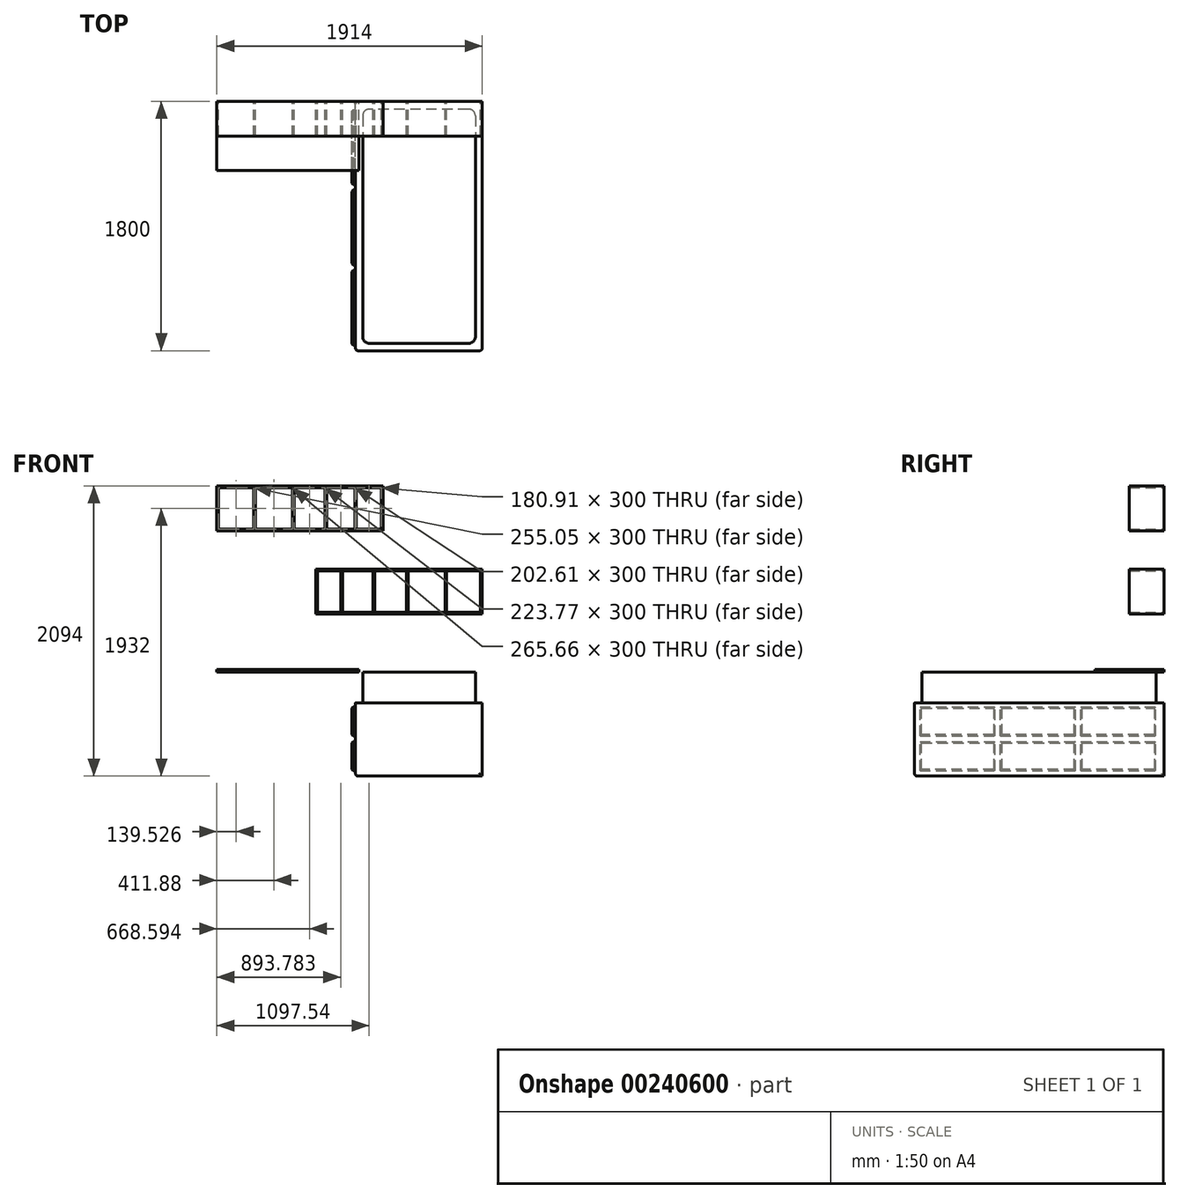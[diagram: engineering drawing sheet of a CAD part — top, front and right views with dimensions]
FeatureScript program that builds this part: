
annotation { "Feature Type Name" : "Feature", "Feature Type Description" : "" }
export const myFeature = defineFeature(function(context is Context, id is Id, definition is map)
    precondition{}
    {
        {
            var Q0;
            Q0=qCreatedBy(makeId("Front.planeOp"),FACE);
            var sketch = newSketch(context, id + "F0", { "sketchPlane" : qUnion([Q0])});
            skLineSegment(sketch, "E0.right", {"start": v(2099, 770) * mm, "end": v(2099, 750) * mm});
            skLineSegment(sketch, "E1.top", {"start": v(2135, 620) * mm, "end": v(2115, 620) * mm});
            skLineSegment(sketch, "E2.bottom", {"start": v(2099, 750) * mm, "end": v(1185, 750) * mm});
            skLineSegment(sketch, "E2.top", {"start": v(2099, 0) * mm, "end": v(1185, 0) * mm});
            skLineSegment(sketch, "E2.left", {"start": v(2099, 750) * mm, "end": v(2099, 0) * mm});
            skLineSegment(sketch, "E2.right", {"start": v(1185, 750) * mm, "end": v(1185, 0) * mm});
            skLineSegment(sketch, "E3.top", {"start": v(2079, 770) * mm, "end": v(2099, 770) * mm});
            skSolve(sketch);
        }
        {
            var Q0;
            {var subQ5=sQuery(id+"F0.wireOp",EDGE,"mjQCl8UT-21zD-DJ05-m4hR-eCqY9wOHKZ8C.bottom");Q0=makeQuery(id+"F0.imprint","IMPRINT",FACE,{"disambiguationData":[TD([[makeQuery(id+"F0.imprint","IMPRINT",EDGE,{"derivedFrom":subQ5}),-1.0]])]});}
            var Q1;
            Q1=makeQuery(id+"F0.imprint","IMPRINT",FACE,{"disambiguationData":[TD([[makeQuery(id+"F0.imprint","IMPRINT",EDGE,{"derivedFrom":sQuery(id+"F0.wireOp",EDGE,"fViOHY5F-jbjT-sDrG-rFHW-0nsrj5jH0THn.bottom")}),1.0]])]});
            var Q2;
            Q2=makeQuery(id+"F0.imprint","IMPRINT",FACE,{"disambiguationData":[TD([[makeQuery(id+"F0.imprint","IMPRINT",EDGE,{"derivedFrom":sQuery(id+"F0.wireOp",EDGE,"CURJZSOY-zp0L-gG35-HGPp-CF3T4XPkt2g1.bottom")}),1.0]])]});
            var Q3;
            Q3=makeQuery(id+"F0.imprint","IMPRINT",FACE,{"disambiguationData":[TD([[makeQuery(id+"F0.imprint","IMPRINT",EDGE,{"derivedFrom":sQuery(id+"F0.wireOp",EDGE,"rYcHEG5W-3RAi-ODDc-aat0-Rc7xTILlibCM.bottom")}),-1.0]])]});
            var Q4;
            {var subQ0=sQuery(id+"F0.wireOp",EDGE,"Hld5sJT8-8Eor-Fkzm-HqOC-IpYSd5zHQiRJ.left");Q4=makeQuery(id+"F0.imprint","IMPRINT",FACE,{"disambiguationData":[TD([[makeQuery(id+"F0.imprint","IMPRINT",EDGE,{"derivedFrom":subQ0}),-1.0]])]});}
            var Q5;
            {var subQ3=sQuery(id+"F0.wireOp",EDGE,"Ef43F33Y-ZOyo-R4mQ-mZii-0W5uo4y5c10D.bottom");Q5=makeQuery(id+"F0.imprint","IMPRINT",FACE,{"disambiguationData":[TD([[makeQuery(id+"F0.imprint","IMPRINT",EDGE,{"derivedFrom":subQ3}),-1.0]])]});}
            var Q6;
            Q6=makeQuery(id+"F0.imprint","IMPRINT",FACE,{"disambiguationData":[TD([[makeQuery(id+"F0.imprint","IMPRINT",EDGE,{"derivedFrom":sQuery(id+"F0.wireOp",EDGE,"NrUvMHko-TrKp-QnW1-jtb7-1sPzA3xdgOMU.bottom")}),-1.0]])]});
            var Q7;
            Q7=makeQuery(id+"F0.imprint","IMPRINT",FACE,{"disambiguationData":[TD([[makeQuery(id+"F0.imprint","IMPRINT",EDGE,{"derivedFrom":sQuery(id+"F0.wireOp",EDGE,"5VmnRn0p-VOUw-hyS7-2uir-4T0axD03U4wE.bottom")}),1.0]])]});
            var Q8;
            {var subQ0=sQuery(id+"F0.wireOp",EDGE,"xXXFPRuC-vsK8-C333-ZqZV-EY1DFygu61gq.bottom");Q8=makeQuery(id+"F0.imprint","IMPRINT",FACE,{"disambiguationData":[TD([[makeQuery(id+"F0.imprint","IMPRINT",EDGE,{"derivedFrom":subQ0}),-1.0]])]});}
            var Q9;
            {var subQ0=sQuery(id+"F0.wireOp",EDGE,"SrouK1QG-l51e-v0bo-YR4G-QEAQBbo4jVZ9.left");Q9=makeQuery(id+"F0.imprint","IMPRINT",FACE,{"disambiguationData":[TD([[makeQuery(id+"F0.imprint","IMPRINT",EDGE,{"derivedFrom":subQ0}),1.0]])]});}
            var Q10;
            {var subQ4=sQuery(id+"F0.wireOp",EDGE,"E3.bottom");Q10=makeQuery(id+"F0.imprint","IMPRINT",FACE,{"disambiguationData":[TD([[makeQuery(id+"F0.imprint","IMPRINT",EDGE,{"derivedFrom":subQ4}),-1.0]])]});}
            var Q11;
            {var subQ5=sQuery(id+"F0.wireOp",EDGE,"E3.top");Q11=makeQuery(id+"F0.imprint","IMPRINT",FACE,{"disambiguationData":[TD([[makeQuery(id+"F0.imprint","IMPRINT",EDGE,{"derivedFrom":subQ5}),1.0]])]});}
            var Q12;
            {var subQ0=sQuery(id+"F0.wireOp",EDGE,"E3.right");var subQ1=sQuery(id+"F0.wireOp",EDGE,"SrouK1QG-l51e-v0bo-YR4G-QEAQBbo4jVZ9.bottom");var subQ2=makeQuery(id+"F0.imprint","INTERSECT",VERTEX,{"derivedFrom":[subQ1,subQ0]});Q12=makeQuery(id+"F0.imprint","IMPRINT",FACE,{"disambiguationData":[TD([[makeQuery(id+"F0.imprint","IMPRINT",EDGE,{"disambiguationData":[TD([[subQ2,1.0]])],"derivedFrom":subQ1}),-1.0]])]});}
            var Q13;
            Q13=makeQuery(id+"F0.imprint","IMPRINT",FACE,{"disambiguationData":[TD([[makeQuery(id+"F0.imprint","IMPRINT",EDGE,{"derivedFrom":sQuery(id+"F0.wireOp",EDGE,"E0.bottom")}),-1.0]])]});
            var Q14;
            Q14=makeQuery(id+"F0.imprint","IMPRINT",FACE,{"disambiguationData":[TD([[makeQuery(id+"F0.imprint","IMPRINT",EDGE,{"derivedFrom":sQuery(id+"F0.wireOp",EDGE,"E2.bottom")}),1.0]])]});
            extrude(context, id + "F1", {"entities" : qUnion([Q0, Q1, Q2, Q3, Q4, Q5, Q6, Q7, Q8, Q9, Q10, Q11, Q12, Q13, Q14]), "depth" : 1800 * mm});
        }
        {
            var Q0;
            Q0=makeQuery(id+"F1.opExtrude","CAP_FACE",FACE,{"disambiguationData":[OSD([sQuery(id+"F0.wireOp",EDGE,"E2.bottom"),sQuery(id+"F0.wireOp",EDGE,"E2.top"),sQuery(id+"F0.wireOp",EDGE,"E2.left"),sQuery(id+"F0.wireOp",EDGE,"E2.right")])],"isStart":true});
            var sketch = newSketch(context, id + "F2", { "sketchPlane" : qUnion([Q0])});
            skLineSegment(sketch, "E4.bottom", {"start": v(-1185, 750) * mm, "end": v(-185, 750) * mm});
            skLineSegment(sketch, "E4.top", {"start": v(-1185, 770) * mm, "end": v(-185, 770) * mm});
            skLineSegment(sketch, "E4.left", {"start": v(-1185, 750) * mm, "end": v(-1185, 770) * mm});
            skLineSegment(sketch, "E4.right", {"start": v(-185, 750) * mm, "end": v(-185, 770) * mm});
            skLineSegment(sketch, "E5.bottom", {"start": v(-1185, 770) * mm, "end": v(-1210, 770) * mm});
            skLineSegment(sketch, "E5.top", {"start": v(-1185, 530) * mm, "end": v(-1210, 530) * mm});
            skLineSegment(sketch, "E5.left", {"start": v(-1185, 770) * mm, "end": v(-1185, 530) * mm});
            skLineSegment(sketch, "E5.right", {"start": v(-1210, 770) * mm, "end": v(-1210, 530) * mm});
            skSolve(sketch);
        }
        {
            var Q0;
            Q0 = qSketchRegion(id + "F2", true);
            extrude(context, id + "F3", {"entities" : qUnion([Q0]), "oppositeDirection" : true, "depth" : 500 * mm});
        }
        {
            var Q0;
            Q0=makeQuery(id+"F1.opExtrude","SWEPT_FACE",FACE,{"disambiguationData":[OSD([sQuery(id+"F0.wireOp",EDGE,"E2.right")])]});
            var sketch = newSketch(context, id + "F4", { "sketchPlane" : qUnion([Q0])});
            skLineSegment(sketch, "E6.bottom", {"start": v(1760, 40) * mm, "end": v(1220, 40) * mm});
            skLineSegment(sketch, "E6.top", {"start": v(1760, 250) * mm, "end": v(1220, 250) * mm});
            skLineSegment(sketch, "E6.left", {"start": v(1760, 40) * mm, "end": v(1760, 250) * mm});
            skLineSegment(sketch, "E6.right", {"start": v(1220, 40) * mm, "end": v(1220, 250) * mm});
            skLineSegment(sketch, "E7.bottom", {"start": v(600, 40) * mm, "end": v(60, 40) * mm});
            skLineSegment(sketch, "E7.top", {"start": v(600, 250) * mm, "end": v(60, 250) * mm});
            skLineSegment(sketch, "E7.left", {"start": v(600, 40) * mm, "end": v(600, 250) * mm});
            skLineSegment(sketch, "E7.right", {"start": v(60, 40) * mm, "end": v(60, 250) * mm});
            skLineSegment(sketch, "E8.bottom", {"start": v(1180, 40) * mm, "end": v(640, 40) * mm});
            skLineSegment(sketch, "E8.top", {"start": v(1180, 250) * mm, "end": v(640, 250) * mm});
            skLineSegment(sketch, "E8.left", {"start": v(1180, 40) * mm, "end": v(1180, 250) * mm});
            skLineSegment(sketch, "E8.right", {"start": v(640, 40) * mm, "end": v(640, 250) * mm});
            skLineSegment(sketch, "E9.0", {"start": v(1800, 750) * mm, "end": v(1800, 0) * mm});
            skLineSegment(sketch, "E10.0", {"start": v(1800, 0) * mm, "end": v(0, 0) * mm});
            skLineSegment(sketch, "E11.bottom", {"start": v(1760, 290) * mm, "end": v(1220, 290) * mm});
            skLineSegment(sketch, "E11.top", {"start": v(1760, 500) * mm, "end": v(1220, 500) * mm});
            skLineSegment(sketch, "E11.left", {"start": v(1760, 290) * mm, "end": v(1760, 500) * mm});
            skLineSegment(sketch, "E11.right", {"start": v(1220, 290) * mm, "end": v(1220, 500) * mm});
            skLineSegment(sketch, "E12.bottom", {"start": v(600, 290) * mm, "end": v(60, 290) * mm});
            skLineSegment(sketch, "E12.top", {"start": v(600, 500) * mm, "end": v(60, 500) * mm});
            skLineSegment(sketch, "E12.left", {"start": v(600, 290) * mm, "end": v(600, 500) * mm});
            skLineSegment(sketch, "E12.right", {"start": v(60, 290) * mm, "end": v(60, 500) * mm});
            skLineSegment(sketch, "E13.bottom", {"start": v(1180, 290) * mm, "end": v(640, 290) * mm});
            skLineSegment(sketch, "E13.top", {"start": v(1180, 500) * mm, "end": v(640, 500) * mm});
            skLineSegment(sketch, "E13.left", {"start": v(1180, 290) * mm, "end": v(1180, 500) * mm});
            skLineSegment(sketch, "E13.right", {"start": v(640, 290) * mm, "end": v(640, 500) * mm});
            skSolve(sketch);
        }
        {
            var Q0;
            Q0 = qSketchRegion(id + "F4", true);
            extrude(context, id + "F5", {"entities" : qUnion([Q0]), "operationType" : NewBodyOperationType.ADD, "depth" : 25 * mm});
        }
        {
            var Q0;
            Q0=makeQuery(id+"F1.opExtrude","SWEPT_FACE",FACE,{"disambiguationData":[OSD([sQuery(id+"F0.wireOp",EDGE,"E2.bottom")])]});
            var sketch = newSketch(context, id + "F6", { "sketchPlane" : qUnion([Q0])});
            skLineSegment(sketch, "E14.bottom", {"start": v(2049.87, -56.11) * mm, "end": v(1236.71, -56.11) * mm});
            skLineSegment(sketch, "E14.top", {"start": v(2049.87, -1747.03) * mm, "end": v(1236.71, -1747.03) * mm});
            skLineSegment(sketch, "E14.left", {"start": v(2049.87, -56.11) * mm, "end": v(2049.87, -1747.03) * mm});
            skLineSegment(sketch, "E14.right", {"start": v(1236.71, -56.11) * mm, "end": v(1236.71, -1747.03) * mm});
            skLineSegment(sketch, "E15.bottom", {"start": v(2099, 0) * mm, "end": v(1185, 0) * mm});
            skLineSegment(sketch, "E15.top", {"start": v(2099, -1800) * mm, "end": v(1185, -1800) * mm});
            skLineSegment(sketch, "E15.left", {"start": v(2099, 0) * mm, "end": v(2099, -1800) * mm});
            skLineSegment(sketch, "E15.right", {"start": v(1185, 0) * mm, "end": v(1185, -1800) * mm});
            skSolve(sketch);
        }
        {
            var Q0;
            Q0=makeQuery(id+"F6.imprint","IMPRINT",FACE,{"disambiguationData":[TD([[makeQuery(id+"F6.imprint","IMPRINT",EDGE,{"derivedFrom":sQuery(id+"F6.wireOp",EDGE,"E14.bottom")}),-1.0]])]});
            extrude(context, id + "F7", {"entities" : qUnion([Q0]), "operationType" : NewBodyOperationType.REMOVE, "oppositeDirection" : true, "depth" : 220 * mm});
        }
        {
            var Q0;
            Q0=makeQuery(id+"F1.opExtrude","CAP_FACE",FACE,{"disambiguationData":[OSD([sQuery(id+"F0.wireOp",EDGE,"E2.bottom"),sQuery(id+"F0.wireOp",EDGE,"E2.top"),sQuery(id+"F0.wireOp",EDGE,"E2.left"),sQuery(id+"F0.wireOp",EDGE,"E2.right")])],"isStart":true});
            var sketch = newSketch(context, id + "F8", { "sketchPlane" : qUnion([Q0])});
            skLineSegment(sketch, "E16.bottom", {"start": v(-2099, 1170) * mm, "end": v(-899, 1170) * mm});
            skLineSegment(sketch, "E16.top", {"start": v(-2099, 1494) * mm, "end": v(-899, 1494) * mm});
            skLineSegment(sketch, "E16.left", {"start": v(-2099, 1170) * mm, "end": v(-2099, 1494) * mm});
            skLineSegment(sketch, "E17.bottom", {"start": v(-2087, 1482) * mm, "end": v(-1843.08, 1482) * mm});
            skLineSegment(sketch, "E17.top", {"start": v(-2087, 1182) * mm, "end": v(-1843.08, 1182) * mm});
            skLineSegment(sketch, "E17.left", {"start": v(-2087, 1482) * mm, "end": v(-2087, 1182) * mm});
            skLineSegment(sketch, "E17.right", {"start": v(-1565.3, 1482) * mm, "end": v(-1565.3, 1182) * mm});
            skLineSegment(sketch, "E18.bottom", {"start": v(-1553.3, 1482) * mm, "end": v(-1322.43, 1482) * mm});
            skLineSegment(sketch, "E18.top", {"start": v(-1553.3, 1182) * mm, "end": v(-1322.43, 1182) * mm});
            skLineSegment(sketch, "E18.left", {"start": v(-1553.3, 1482) * mm, "end": v(-1553.3, 1182) * mm});
            skLineSegment(sketch, "E18.right", {"start": v(-1322.43, 1482) * mm, "end": v(-1322.43, 1182) * mm});
            skLineSegment(sketch, "E19.bottom", {"start": v(-1310.43, 1482) * mm, "end": v(-1092.16, 1482) * mm});
            skLineSegment(sketch, "E19.top", {"start": v(-1310.43, 1182) * mm, "end": v(-1092.16, 1182) * mm});
            skLineSegment(sketch, "E19.left", {"start": v(-1310.43, 1482) * mm, "end": v(-1310.43, 1182) * mm});
            skLineSegment(sketch, "E19.right", {"start": v(-1092.16, 1482) * mm, "end": v(-1092.16, 1182) * mm});
            skLineSegment(sketch, "E20.bottom", {"start": v(-1080.16, 1482) * mm, "end": v(-911, 1482) * mm});
            skLineSegment(sketch, "E20.top", {"start": v(-1080.16, 1182) * mm, "end": v(-911, 1182) * mm});
            skLineSegment(sketch, "E20.left", {"start": v(-1080.16, 1482) * mm, "end": v(-1080.16, 1182) * mm});
            skLineSegment(sketch, "E20.right", {"start": v(-911, 1482) * mm, "end": v(-911, 1182) * mm});
            skLineSegment(sketch, "E21", {"start": v(-899, 1494) * mm, "end": v(-899, 1170) * mm});
            skLineSegment(sketch, "E22.left", {"start": v(-1831.08, 1482) * mm, "end": v(-1831.08, 1182) * mm});
            skLineSegment(sketch, "E22.right", {"start": v(-1843.08, 1482) * mm, "end": v(-1843.08, 1182) * mm});
            skLineSegment(sketch, "E23.0", {"start": v(-2099, 530) * mm, "end": v(-2099, 0) * mm});
            skLineSegment(sketch, "E24.0", {"start": v(-185, 770) * mm, "end": v(-185, 770) * mm});
            skLineSegment(sketch, "E25.bottom", {"start": v(-1385, 1770) * mm, "end": v(-185, 1770) * mm});
            skLineSegment(sketch, "E25.top", {"start": v(-1385, 2094) * mm, "end": v(-185, 2094) * mm});
            skLineSegment(sketch, "E25.left", {"start": v(-1385, 1770) * mm, "end": v(-1385, 2094) * mm});
            skLineSegment(sketch, "E26.left", {"start": v(-1373, 2082) * mm, "end": v(-1373, 1782) * mm});
            skLineSegment(sketch, "E26.right", {"start": v(-464.05, 2082) * mm, "end": v(-464.05, 1782) * mm});
            skLineSegment(sketch, "E27.left", {"start": v(-452.05, 2082) * mm, "end": v(-452.05, 1782) * mm});
            skLineSegment(sketch, "E27.right", {"start": v(-741.7, 2082) * mm, "end": v(-741.7, 1782) * mm});
            skLineSegment(sketch, "E28.left", {"start": v(-729.7, 2082) * mm, "end": v(-729.7, 1782) * mm});
            skLineSegment(sketch, "E28.right", {"start": v(-977.48, 2082) * mm, "end": v(-977.48, 1782) * mm});
            skLineSegment(sketch, "E29.left", {"start": v(-965.48, 2082) * mm, "end": v(-965.48, 1782) * mm});
            skLineSegment(sketch, "E29.right", {"start": v(-197, 2082) * mm, "end": v(-197, 1782) * mm});
            skLineSegment(sketch, "E30", {"start": v(-185, 2094) * mm, "end": v(-185, 1770) * mm});
            skLineSegment(sketch, "E31.left", {"start": v(-1180.09, 2082) * mm, "end": v(-1180.09, 1782) * mm});
            skLineSegment(sketch, "E31.right", {"start": v(-1192.09, 2082) * mm, "end": v(-1192.09, 1782) * mm});
            skPoint(sketch, "E32.0", {"position": v(-185, 760) * mm});
            skLineSegment(sketch, "E33.0", {"start": v(-185, 750) * mm, "end": v(-185, 770) * mm});
            skLineSegment(sketch, "E34", {"start": v(-1373, 1782) * mm, "end": v(-1192.09, 1782) * mm});
            skLineSegment(sketch, "E35", {"start": v(-1373, 2082) * mm, "end": v(-1192.09, 2082) * mm});
            skLineSegment(sketch, "E36", {"start": v(-1180.09, 2082) * mm, "end": v(-977.48, 2082) * mm});
            skLineSegment(sketch, "E37", {"start": v(-965.48, 2082) * mm, "end": v(-741.7, 2082) * mm});
            skLineSegment(sketch, "E38", {"start": v(-729.7, 2082) * mm, "end": v(-464.05, 2082) * mm});
            skLineSegment(sketch, "E39", {"start": v(-464.05, 1782) * mm, "end": v(-729.7, 1782) * mm});
            skLineSegment(sketch, "E40", {"start": v(-741.7, 1782) * mm, "end": v(-965.48, 1782) * mm});
            skLineSegment(sketch, "E41", {"start": v(-977.48, 1782) * mm, "end": v(-1180.09, 1782) * mm});
            skLineSegment(sketch, "E42", {"start": v(-452.05, 2082) * mm, "end": v(-197, 2082) * mm});
            skLineSegment(sketch, "E43", {"start": v(-197, 1782) * mm, "end": v(-452.05, 1782) * mm});
            skLineSegment(sketch, "E44.trimOffspring", {"start": v(-1831.08, 1182) * mm, "end": v(-1565.3, 1182) * mm});
            skLineSegment(sketch, "E45.trimOffspring", {"start": v(-1831.08, 1482) * mm, "end": v(-1565.3, 1482) * mm});
            skSolve(sketch);
        }
        {
            var Q0;
            Q0 = qSketchRegion(id + "F8", true);
            extrude(context, id + "F9", {"entities" : qUnion([Q0]), "oppositeDirection" : true, "depth" : 250 * mm});
        }
        {
            var Q0;
            Q0 = qSketchRegion(id + "F4", true);
            extrude(context, id + "F10", {"entities" : qUnion([Q0]), "operationType" : NewBodyOperationType.ADD, "depth" : 25 * mm});
        }
        {
            var Q0;
            Q0=makeQuery(id+"F7.boolean.opBoolean","COPY",EDGE,{"derivedFrom":makeQuery(id+"F7.opExtrude","CAP_EDGE",EDGE,{"disambiguationData":[OSD([sQuery(id+"F6.wireOp",EDGE,"E15.top")])],"isStart":false})});
            var Q1;
            Q1=makeQuery(id+"F7.boolean.opBoolean","COPY",EDGE,{"derivedFrom":makeQuery(id+"F7.opExtrude","CAP_EDGE",EDGE,{"disambiguationData":[OSD([sQuery(id+"F6.wireOp",EDGE,"E15.right")])],"isStart":false})});
            var Q2;
            Q2=makeQuery(id+"F1.opExtrude","CAP_EDGE",EDGE,{"disambiguationData":[OSD([sQuery(id+"F0.wireOp",EDGE,"E2.right")])],"isStart":false});
            var Q3;
            Q3=makeQuery(id+"F1.opExtrude","CAP_EDGE",EDGE,{"disambiguationData":[OSD([sQuery(id+"F0.wireOp",EDGE,"E2.right")])],"isStart":true});
            var Q4;
            Q4=makeQuery(id+"F7.boolean.opBoolean","COPY",EDGE,{"derivedFrom":makeQuery(id+"F7.opExtrude","CAP_EDGE",EDGE,{"disambiguationData":[OSD([sQuery(id+"F6.wireOp",EDGE,"E15.bottom")])],"isStart":false})});
            var Q5;
            Q5=makeQuery(id+"F1.opExtrude","CAP_EDGE",EDGE,{"disambiguationData":[OSD([sQuery(id+"F0.wireOp",EDGE,"E2.top")])],"isStart":false});
            var Q6;
            Q6=makeQuery(id+"F1.opExtrude","SWEPT_EDGE",EDGE,{"disambiguationData":[OSD([sQuery(id+"F0.wireOp",EDGE,"E2.top"),sQuery(id+"F0.wireOp",EDGE,"E2.right")])]});
            var Q7;
            Q7=makeQuery(id+"F7.boolean.opBoolean","COPY",EDGE,{"derivedFrom":makeQuery(id+"F7.opExtrude","CAP_EDGE",EDGE,{"disambiguationData":[OSD([sQuery(id+"F6.wireOp",EDGE,"E15.left")])],"isStart":false})});
            var Q8;
            Q8=makeQuery(id+"F1.opExtrude","CAP_EDGE",EDGE,{"disambiguationData":[OSD([sQuery(id+"F0.wireOp",EDGE,"E2.left")])],"isStart":false});
            fillet(context, id + "F11", {"entities" : qUnion([Q0, Q1, Q2, Q3, Q4, Q5, Q6, Q7, Q8]), "radius" : 20 * mm, "tangentPropagation" : true, "allowEdgeOverflow" : false});
        }
        {
            var Q0;
            Q0=makeQuery(id+"F7.boolean.opBoolean","COPY",EDGE,{"derivedFrom":makeQuery(id+"F7.opExtrude","CAP_EDGE",EDGE,{"disambiguationData":[OSD([sQuery(id+"F6.wireOp",EDGE,"E14.right")])],"isStart":true})});
            var Q1;
            Q1=makeQuery(id+"F7.boolean.opBoolean","COPY",EDGE,{"derivedFrom":makeQuery(id+"F7.opExtrude","CAP_EDGE",EDGE,{"disambiguationData":[OSD([sQuery(id+"F6.wireOp",EDGE,"E14.top")])],"isStart":true})});
            var Q2;
            Q2=makeQuery(id+"F7.boolean.opBoolean","COPY",EDGE,{"derivedFrom":makeQuery(id+"F7.opExtrude","SWEPT_EDGE",EDGE,{"disambiguationData":[OSD([sQuery(id+"F6.wireOp",EDGE,"E14.top"),sQuery(id+"F6.wireOp",EDGE,"E14.right")])]})});
            var Q3;
            Q3=makeQuery(id+"F7.boolean.opBoolean","COPY",EDGE,{"derivedFrom":makeQuery(id+"F7.opExtrude","SWEPT_EDGE",EDGE,{"disambiguationData":[OSD([sQuery(id+"F6.wireOp",EDGE,"E14.top"),sQuery(id+"F6.wireOp",EDGE,"E14.left")])]})});
            var Q4;
            Q4=makeQuery(id+"F7.boolean.opBoolean","COPY",EDGE,{"derivedFrom":makeQuery(id+"F7.opExtrude","CAP_EDGE",EDGE,{"disambiguationData":[OSD([sQuery(id+"F6.wireOp",EDGE,"E14.left")])],"isStart":true})});
            var Q5;
            Q5=makeQuery(id+"F7.boolean.opBoolean","COPY",EDGE,{"derivedFrom":makeQuery(id+"F7.opExtrude","CAP_EDGE",EDGE,{"disambiguationData":[OSD([sQuery(id+"F6.wireOp",EDGE,"E14.bottom")])],"isStart":true})});
            var Q6;
            Q6=makeQuery(id+"F7.boolean.opBoolean","COPY",EDGE,{"derivedFrom":makeQuery(id+"F7.opExtrude","SWEPT_EDGE",EDGE,{"disambiguationData":[OSD([sQuery(id+"F6.wireOp",EDGE,"E14.bottom"),sQuery(id+"F6.wireOp",EDGE,"E14.left")])]})});
            var Q7;
            Q7=makeQuery(id+"F7.boolean.opBoolean","COPY",EDGE,{"derivedFrom":makeQuery(id+"F7.opExtrude","SWEPT_EDGE",EDGE,{"disambiguationData":[OSD([sQuery(id+"F6.wireOp",EDGE,"E14.bottom"),sQuery(id+"F6.wireOp",EDGE,"E14.right")])]})});
            fillet(context, id + "F12", {"entities" : qUnion([Q0, Q1, Q2, Q3, Q4, Q5, Q6, Q7]), "radius" : 50 * mm, "tangentPropagation" : true, "allowEdgeOverflow" : false});
        }
        {
            var Q0;
            Q0=makeQuery(id+"F5.opExtrude","CAP_FACE",FACE,{"disambiguationData":[OSD([sQuery(id+"F4.wireOp",EDGE,"E12.bottom"),sQuery(id+"F4.wireOp",EDGE,"E12.top"),sQuery(id+"F4.wireOp",EDGE,"E12.left"),sQuery(id+"F4.wireOp",EDGE,"E12.right")])],"isStart":false});
            var Q1;
            Q1=makeQuery(id+"F5.opExtrude","CAP_FACE",FACE,{"disambiguationData":[OSD([sQuery(id+"F4.wireOp",EDGE,"E13.bottom"),sQuery(id+"F4.wireOp",EDGE,"E13.top"),sQuery(id+"F4.wireOp",EDGE,"E13.left"),sQuery(id+"F4.wireOp",EDGE,"E13.right")])],"isStart":false});
            var Q2;
            Q2=makeQuery(id+"F5.opExtrude","CAP_FACE",FACE,{"disambiguationData":[OSD([sQuery(id+"F4.wireOp",EDGE,"E11.bottom"),sQuery(id+"F4.wireOp",EDGE,"E11.top"),sQuery(id+"F4.wireOp",EDGE,"E11.left"),sQuery(id+"F4.wireOp",EDGE,"E11.right")])],"isStart":false});
            var Q3;
            Q3=makeQuery(id+"F5.opExtrude","CAP_FACE",FACE,{"disambiguationData":[OSD([sQuery(id+"F4.wireOp",EDGE,"E6.bottom"),sQuery(id+"F4.wireOp",EDGE,"E6.top"),sQuery(id+"F4.wireOp",EDGE,"E6.left"),sQuery(id+"F4.wireOp",EDGE,"E6.right")])],"isStart":false});
            var Q4;
            Q4=makeQuery(id+"F5.opExtrude","CAP_FACE",FACE,{"disambiguationData":[OSD([sQuery(id+"F4.wireOp",EDGE,"E8.bottom"),sQuery(id+"F4.wireOp",EDGE,"E8.top"),sQuery(id+"F4.wireOp",EDGE,"E8.left"),sQuery(id+"F4.wireOp",EDGE,"E8.right")])],"isStart":false});
            var Q5;
            Q5=makeQuery(id+"F5.opExtrude","CAP_FACE",FACE,{"disambiguationData":[OSD([sQuery(id+"F4.wireOp",EDGE,"E7.bottom"),sQuery(id+"F4.wireOp",EDGE,"E7.top"),sQuery(id+"F4.wireOp",EDGE,"E7.left"),sQuery(id+"F4.wireOp",EDGE,"E7.right")])],"isStart":false});
            chamfer(context, id + "F13", {"entities" : qUnion([Q0, Q1, Q2, Q3, Q4, Q5]), "width" : 10 * mm, "tangentPropagation" : true});
        }
    });
